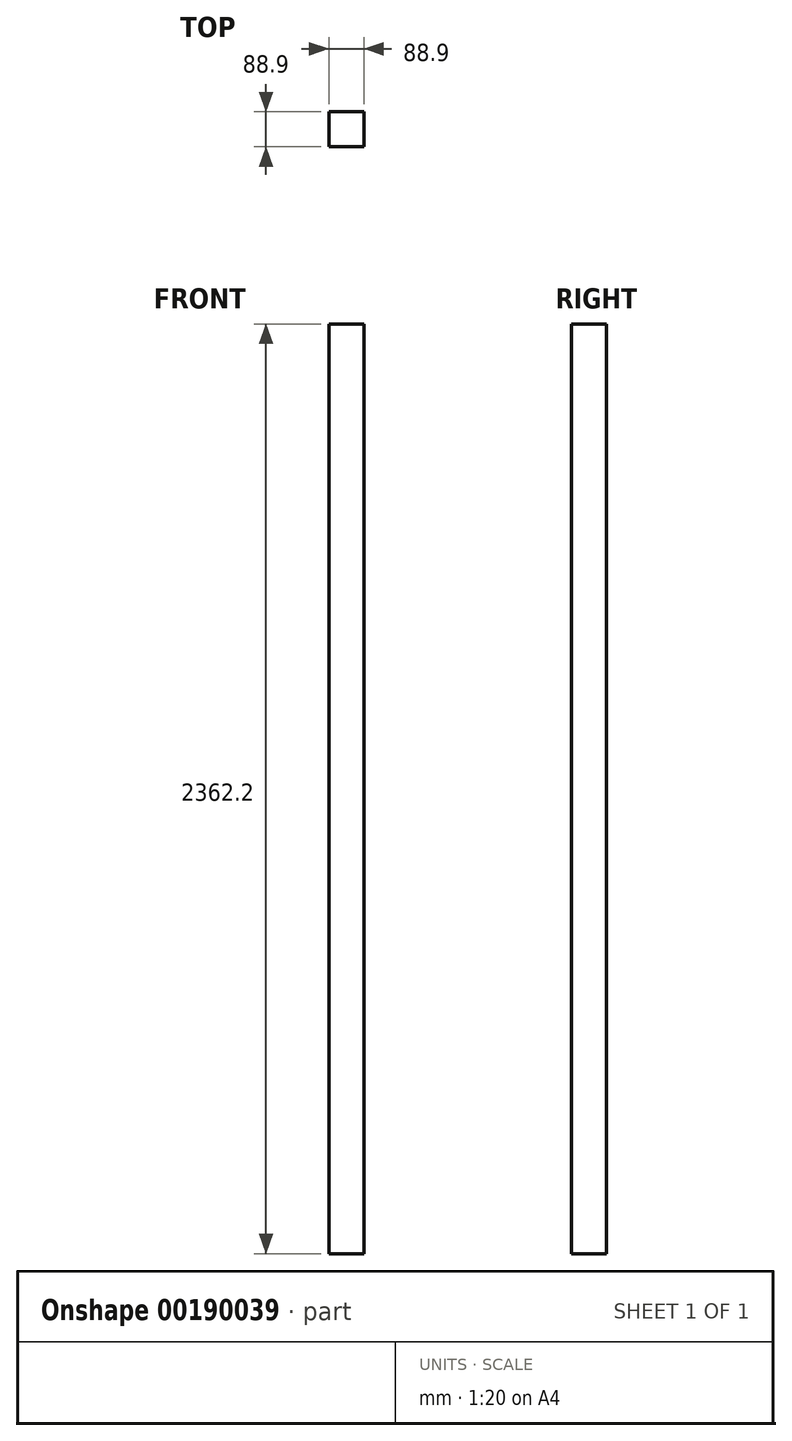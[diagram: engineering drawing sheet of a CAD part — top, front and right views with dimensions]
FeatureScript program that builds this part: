
annotation { "Feature Type Name" : "Feature", "Feature Type Description" : "" }
export const myFeature = defineFeature(function(context is Context, id is Id, definition is map)
    precondition{}
    {
        {
            var Q0;
            Q0=qCreatedBy(makeId("Top.planeOp"),FACE);
            var sketch = newSketch(context, id + "F1", { "sketchPlane" : qUnion([Q0])});
            skLineSegment(sketch, "E0.bottom", {"start": v(44.45, 44.45) * mm, "end": v(-44.45, 44.45) * mm});
            skLineSegment(sketch, "E0.top", {"start": v(44.45, -44.45) * mm, "end": v(-44.45, -44.45) * mm});
            skLineSegment(sketch, "E0.left", {"start": v(44.45, 44.45) * mm, "end": v(44.45, -44.45) * mm});
            skLineSegment(sketch, "E0.right", {"start": v(-44.45, 44.45) * mm, "end": v(-44.45, -44.45) * mm});
            skPoint(sketch, "E0.middle", {"position": v(0, 0) * mm});
            skSolve(sketch);
        }
        {
            var Q0;
            Q0 = qSketchRegion(id + "F1", true);
            extrude(context, id + "F0", {"entities" : qUnion([Q0]), "depth" : 2362.2 * mm});
        }
    });
